# Revit family: desiree
name_source: partatom
category: Furniture
revit_build: Autodesk Revit 2015 (Build: 20140903_1530(x64)
units: mm (PartAtom-declared; Revit-internal decimal feet)

## types (9) — shared parameters
BIMobject category = Furniture
Date of publishing = 2015-07-21
Design country = Sweden
Edition number = 1
IFC Classification = Furniture
Manufacturer country = Sweden
Manufacturer name = Swedese
Material main = Laminate
Material secondary = Steel
Nominal height = 720
Product Guid = 4893596a-c508-4945-8c2c-41bbb65696bb
Product SKU = 23625
Product data url = https://bimobject.com
Product family = Tables
Product group = Desir??e
Product name = Desir??e
QR code = http://bimobject.com
Technical description = https://static-swedese.s3.amazonaws.com
UNSPSC Code = 56
Uniclass 1.4 Code = L8211
Uniclass 1.4 Description = Furniture
Weight Net (Kg) = 24
zero-valued in all types: BOSUseNativeGeometries, Nominal width

## per-type parameters (varying)
| type | Diam 186 | Diam 64 | Diam110 |
| TYPE - (Desire 1860) COLOUR - (Dark Brown) | Yes | No | No |
| TYPE - (Desire 1100) COLOUR - (Dark Brown) | No | No | Yes |
| TYPE - (Desire 640) COLOUR - (Dark Brown) | No | Yes | No |
| TYPE - (Desire 1860) COLOUR - (Light Brown) | Yes | No | No |
| TYPE - (Desire 1100) COLOUR - (Light Brown) | No | No | Yes |
| TYPE - (Desire 640) COLOUR - (Light Brown) | No | Yes | No |
| TYPE - (Desire 1860) COLOUR - (Greenish) | Yes | No | No |
| TYPE - (Desire 1100) COLOUR - (Greenish) | No | No | Yes |
| TYPE - (Desire 640) COLOUR - (Greenish) | No | Yes | No |

## geometry (parser evidence)
native form markers: Sweep x1
no freeform markers — native parametric forms only
